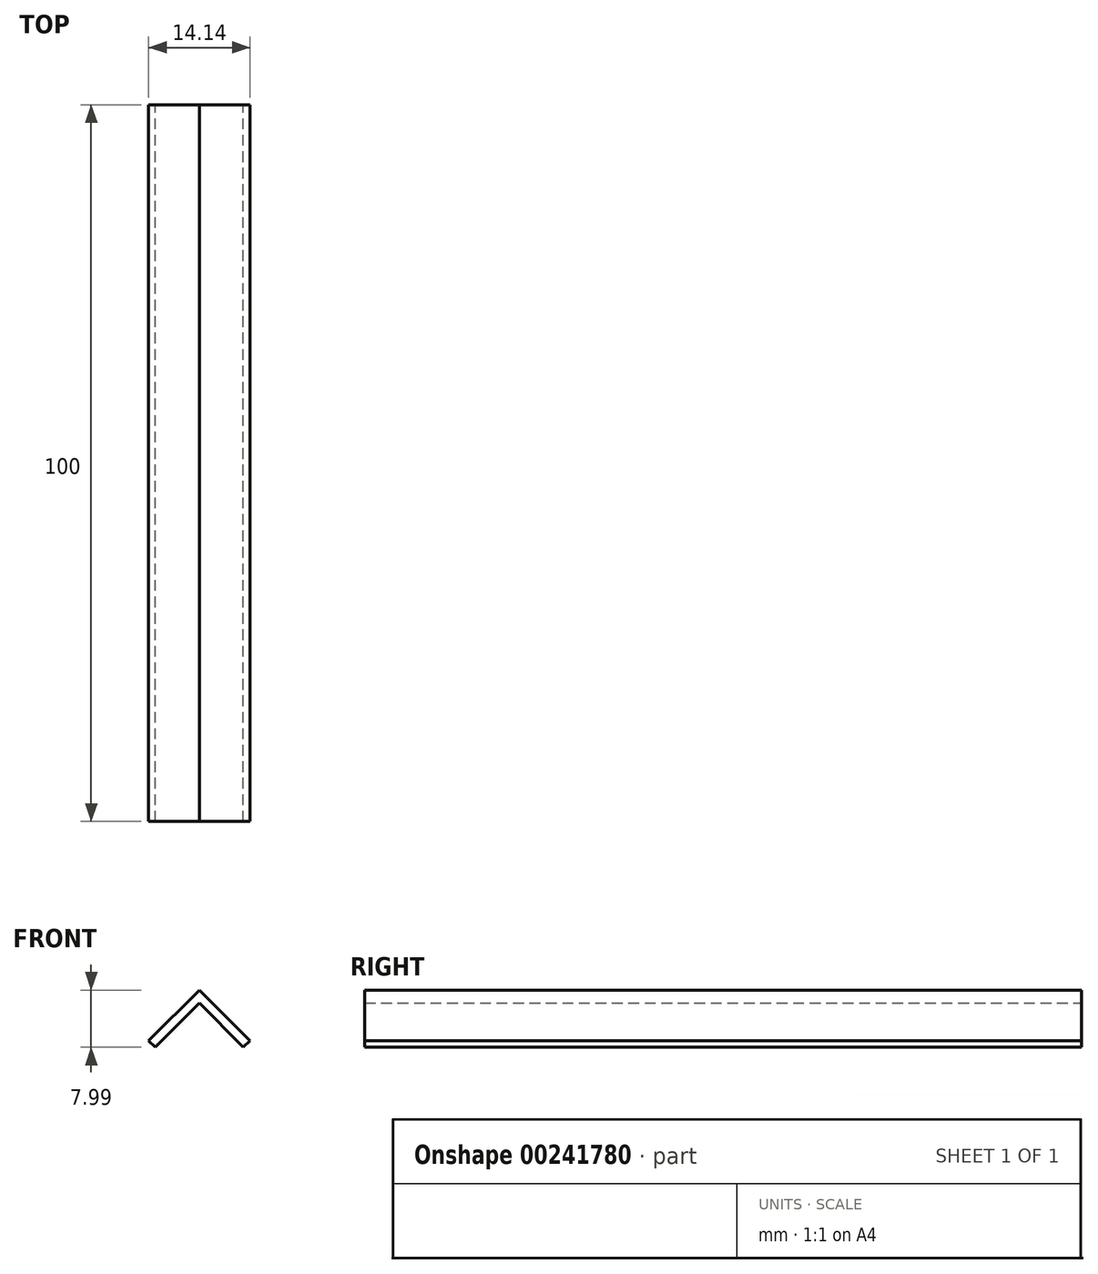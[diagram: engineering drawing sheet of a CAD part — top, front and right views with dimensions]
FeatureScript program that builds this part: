
annotation { "Feature Type Name" : "Feature", "Feature Type Description" : "" }
export const myFeature = defineFeature(function(context is Context, id is Id, definition is map)
    precondition{}
    {
        {
            var Q0;
            Q0=qCreatedBy(makeId("Front.planeOp"),FACE);
            var sketch = newSketch(context, id + "F0", { "sketchPlane" : qUnion([Q0])});
            skLineSegment(sketch, "E0", {"start": v(0, 0) * mm, "end": v(7.07, 7.07) * mm});
            skLineSegment(sketch, "E1", {"start": v(7.07, 7.07) * mm, "end": v(14.14, 0) * mm});
            skLineSegment(sketch, "E2", {"start": v(14.14, 0) * mm, "end": v(13.22, -0.92) * mm});
            skLineSegment(sketch, "E3", {"start": v(13.22, -0.92) * mm, "end": v(7.07, 5.23) * mm});
            skLineSegment(sketch, "E4", {"start": v(7.07, 5.23) * mm, "end": v(0.92, -0.92) * mm});
            skLineSegment(sketch, "E5", {"start": v(0.92, -0.92) * mm, "end": v(0, 0) * mm});
            skSolve(sketch);
        }
        {
            var Q0;
            Q0 = qSketchRegion(id + "F0", true);
            extrude(context, id + "F1", {"entities" : qUnion([Q0]), "depth" : 100 * mm});
        }
    });
